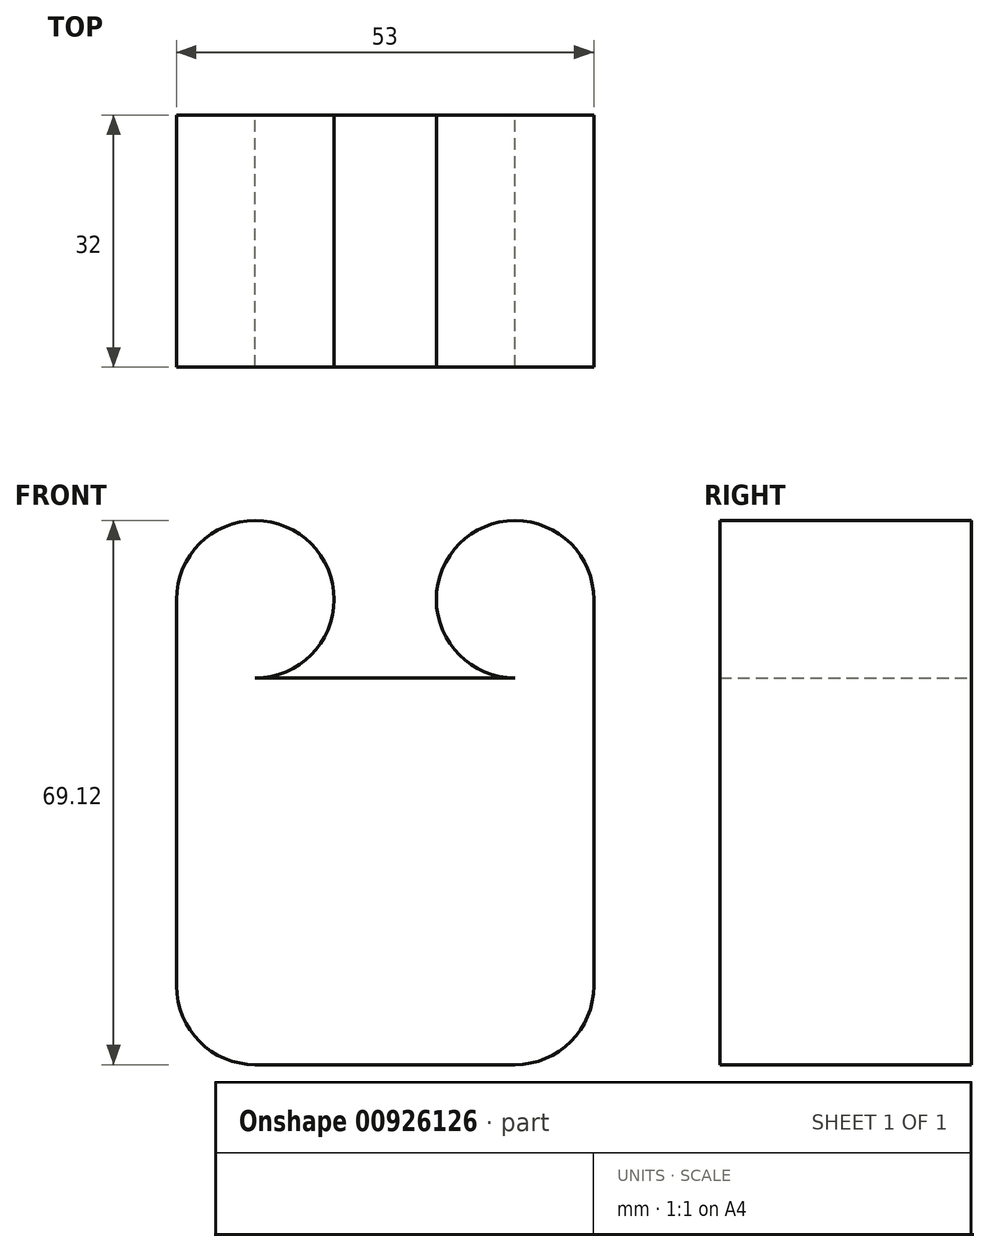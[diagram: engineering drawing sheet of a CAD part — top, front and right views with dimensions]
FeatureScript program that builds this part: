
annotation { "Feature Type Name" : "Feature", "Feature Type Description" : "" }
export const myFeature = defineFeature(function(context is Context, id is Id, definition is map)
    precondition{}
    {
        {
            var Q0;
            Q0=qCreatedBy(makeId("Front.planeOp"),FACE);
            var sketch = newSketch(context, id + "F0", { "sketchPlane" : qUnion([Q0])});
            skLineSegment(sketch, "E0", {"start": v(-12.02, 15.67) * mm, "end": v(20.98, 15.67) * mm});
            skLineSegment(sketch, "E1", {"start": v(-22.02, 25.67) * mm, "end": v(-22.02, -23.45) * mm});
            skLineSegment(sketch, "E2", {"start": v(-12.02, -33.45) * mm, "end": v(20.98, -33.45) * mm});
            skLineSegment(sketch, "E3", {"start": v(30.98, -23.45) * mm, "end": v(30.98, 25.67) * mm});
            skArc(sketch, "E4.filletArc", {"start": v(-12.02, 15.67) * mm, "mid": v(-4.95, 32.74) * mm, "end": v(-22.02, 25.67) * mm});
            skArc(sketch, "E5.filletArc", {"start": v(-22.02, -23.45) * mm, "mid": v(-19.09, -30.52) * mm, "end": v(-12.02, -33.45) * mm});
            skArc(sketch, "E6.filletArc", {"start": v(30.98, 25.67) * mm, "mid": v(13.91, 32.74) * mm, "end": v(20.98, 15.67) * mm});
            skArc(sketch, "E7.filletArc", {"start": v(20.98, -33.45) * mm, "mid": v(28.05, -30.52) * mm, "end": v(30.98, -23.45) * mm});
            skSolve(sketch);
        }
        {
            var Q0;
            Q0=makeQuery(id+"F0.imprint","IMPRINT",FACE,{"disambiguationData":[TD([[makeQuery(id+"F0.imprint","IMPRINT",EDGE,{"derivedFrom":sQuery(id+"F0.wireOp",EDGE,"E0")}),-1.0]])]});
            extrude(context, id + "F1", {"entities" : qUnion([Q0]), "depth" : 32 * mm, "offsetDistance" : 25 * mm});
        }
    });
